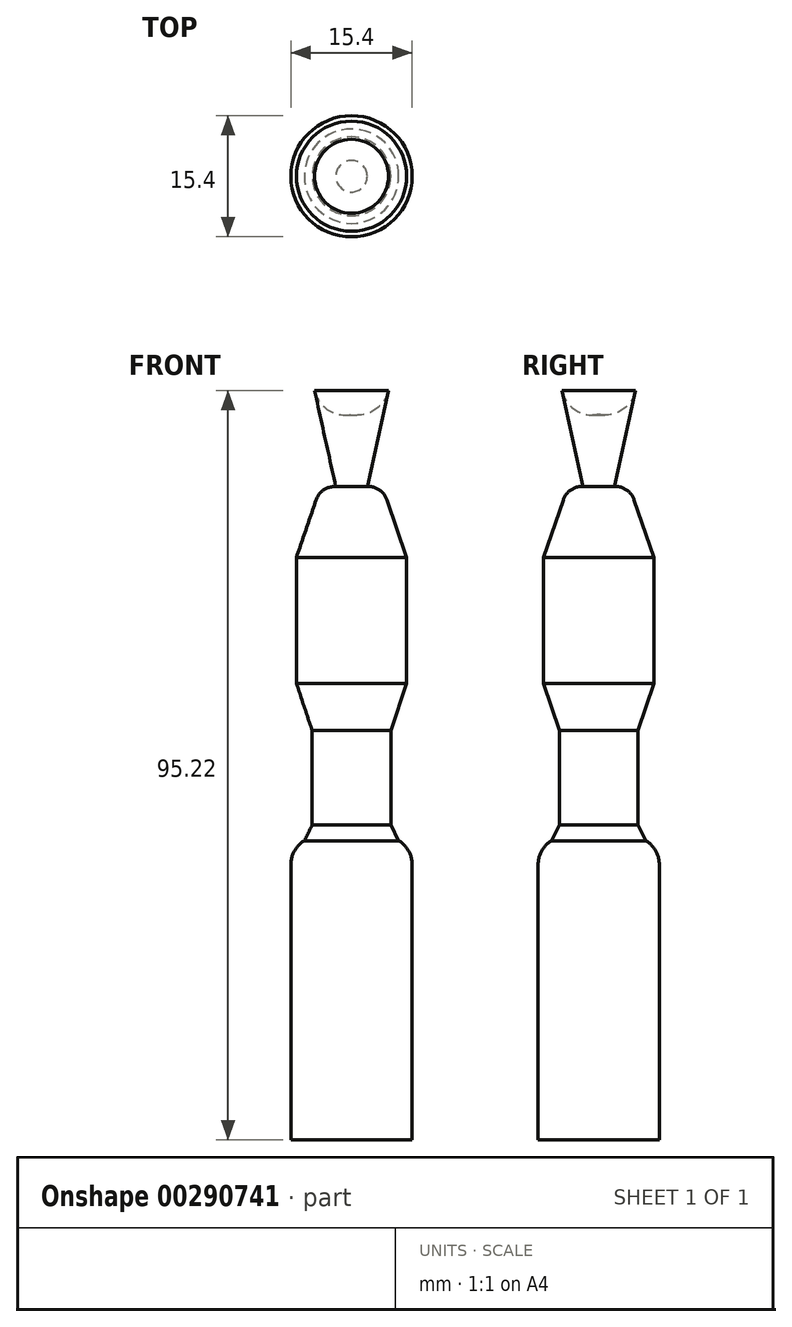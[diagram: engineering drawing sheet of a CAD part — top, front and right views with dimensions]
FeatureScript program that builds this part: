
annotation { "Feature Type Name" : "Feature", "Feature Type Description" : "" }
export const myFeature = defineFeature(function(context is Context, id is Id, definition is map)
    precondition{}
    {
        {
            var Q0;
            Q0=qCreatedBy(makeId("Front.planeOp"),FACE);
            var sketch = newSketch(context, id + "F0", { "sketchPlane" : qUnion([Q0])});
            skArc(sketch, "E0", {"start": v(4.7, -4.78) * mm, "mid": v(3.65, -1.12) * mm, "end": v(0, 0) * mm});
            skLineSegment(sketch, "E1", {"start": v(4.7, -4.78) * mm, "end": v(2, -17) * mm});
            skLineSegment(sketch, "E2", {"start": v(0, 0) * mm, "end": v(0, -109.16) * mm, "construction": true});
            skArc(sketch, "E3", {"start": v(4.5, -18.69) * mm, "mid": v(3.53, -17.42) * mm, "end": v(2, -17) * mm});
            skLineSegment(sketch, "E4", {"start": v(4.5, -18.69) * mm, "end": v(7, -26) * mm});
            skLineSegment(sketch, "E5", {"start": v(7, -26) * mm, "end": v(7, -42) * mm});
            skLineSegment(sketch, "E6", {"start": v(7, -42) * mm, "end": v(5, -48) * mm});
            skLineSegment(sketch, "E7", {"start": v(5, -48) * mm, "end": v(5, -60) * mm});
            skLineSegment(sketch, "E8", {"start": v(5, -60) * mm, "end": v(6, -62) * mm});
            skArc(sketch, "E9", {"start": v(7.7, -65) * mm, "mid": v(7.24, -63.28) * mm, "end": v(6, -62) * mm});
            skLineSegment(sketch, "E10", {"start": v(7.7, -65) * mm, "end": v(7.7, -100) * mm});
            skLineSegment(sketch, "E11", {"start": v(7.7, -100) * mm, "end": v(0, -100) * mm});
            skSolve(sketch);
        }
        {
            var Q0;
            Q0=sQuery(id+"F0.wireOp",EDGE,"E10");
            var Q1;
            Q1=sQuery(id+"F0.wireOp",EDGE,"E6");
            var Q2;
            Q2=sQuery(id+"F0.wireOp",EDGE,"E11");
            var Q3;
            Q3=sQuery(id+"F0.wireOp",EDGE,"E7");
            var Q4;
            Q4=sQuery(id+"F0.wireOp",EDGE,"E5");
            var Q5;
            Q5=sQuery(id+"F0.wireOp",EDGE,"E4");
            var Q6;
            Q6=sQuery(id+"F0.wireOp",EDGE,"E1");
            var Q7;
            Q7=sQuery(id+"F0.wireOp",EDGE,"E0");
            var Q8;
            Q8=sQuery(id+"F0.wireOp",EDGE,"E9");
            var Q9;
            Q9=sQuery(id+"F0.wireOp",EDGE,"E8");
            var Q10;
            Q10=sQuery(id+"F0.wireOp",EDGE,"E3");
            var Q11;
            Q11=sQuery(id+"F0.wireOp",EDGE,"E2");
            revolve(context, id + "F1", {"bodyType" : ToolBodyType.SURFACE, "surfaceEntities" : qUnion([Q0, Q1, Q2, Q3, Q4, Q5, Q6, Q7, Q8, Q9, Q10]), "axis" : qUnion([Q11]), "revolveType" : RevolveType.FULL});
        }
    });
